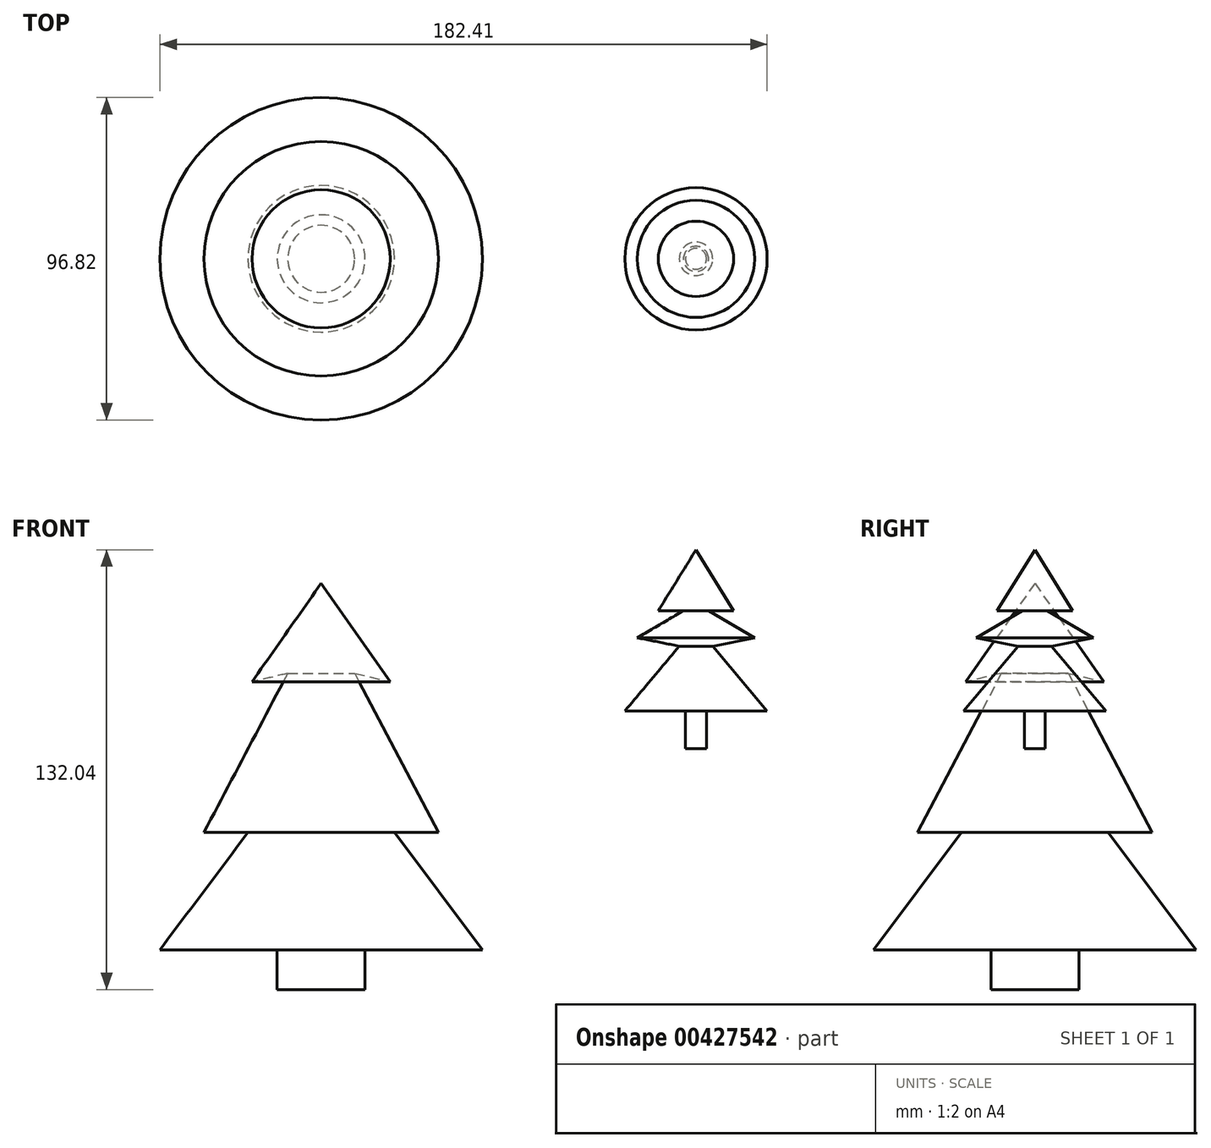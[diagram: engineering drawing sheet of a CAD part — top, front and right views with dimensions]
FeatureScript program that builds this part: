
annotation { "Feature Type Name" : "Feature", "Feature Type Description" : "" }
export const myFeature = defineFeature(function(context is Context, id is Id, definition is map)
    precondition{}
    {
        {
            var Q0;
            Q0=qCreatedBy(makeId("Front.planeOp"),FACE);
            var sketch = newSketch(context, id + "F0", { "sketchPlane" : qUnion([Q0])});
            skLineSegment(sketch, "E0", {"start": v(-35.21, 55.49) * mm, "end": v(-55.96, 25.94) * mm});
            skLineSegment(sketch, "E1", {"start": v(-55.96, 25.94) * mm, "end": v(-45.27, 28.45) * mm});
            skLineSegment(sketch, "E2", {"start": v(-45.27, 28.45) * mm, "end": v(-70.42, -19.33) * mm});
            skLineSegment(sketch, "E3", {"start": v(-70.42, -19.33) * mm, "end": v(-57.22, -19.33) * mm});
            skLineSegment(sketch, "E4", {"start": v(-57.22, -19.33) * mm, "end": v(-83.63, -54.55) * mm});
            skLineSegment(sketch, "E5", {"start": v(-83.63, -54.55) * mm, "end": v(-48.41, -54.55) * mm});
            skLineSegment(sketch, "E6", {"start": v(-35.21, -54.55) * mm, "end": v(-35.21, 55.49) * mm});
            skLineSegment(sketch, "E7", {"start": v(-48.41, -54.55) * mm, "end": v(-48.41, -66.5) * mm});
            skLineSegment(sketch, "E8", {"start": v(-48.41, -66.5) * mm, "end": v(-35.21, -66.5) * mm});
            skLineSegment(sketch, "E9", {"start": v(-35.21, -66.5) * mm, "end": v(-35.21, -54.55) * mm});
            skLineSegment(sketch, "E10", {"start": v(77.4, 65.55) * mm, "end": v(66.08, 47.31) * mm});
            skLineSegment(sketch, "E11", {"start": v(66.08, 47.31) * mm, "end": v(73.63, 47.31) * mm});
            skLineSegment(sketch, "E12", {"start": v(73.63, 47.31) * mm, "end": v(59.8, 39.14) * mm});
            skLineSegment(sketch, "E13", {"start": v(59.8, 39.14) * mm, "end": v(72.37, 36.63) * mm});
            skLineSegment(sketch, "E14", {"start": v(72.37, 36.63) * mm, "end": v(56.02, 17.13) * mm});
            skLineSegment(sketch, "E15", {"start": v(56.02, 17.13) * mm, "end": v(74.25, 17.13) * mm});
            skLineSegment(sketch, "E16", {"start": v(74.25, 17.13) * mm, "end": v(74.25, 5.82) * mm});
            skLineSegment(sketch, "E17", {"start": v(74.25, 5.82) * mm, "end": v(77.4, 5.82) * mm});
            skLineSegment(sketch, "E18", {"start": v(77.4, 5.82) * mm, "end": v(77.4, 65.55) * mm});
            skSolve(sketch);
        }
        {
            var Q0;
            Q0=makeQuery(id+"F0.imprint","IMPRINT",FACE,{"disambiguationData":[TD([[makeQuery(id+"F0.imprint","IMPRINT",EDGE,{"derivedFrom":sQuery(id+"F0.wireOp",EDGE,"E0")}),1.0]])]});
            var Q1;
            Q1=sQuery(id+"F0.wireOp",EDGE,"E6");
            revolve(context, id + "F1", {"entities" : qUnion([Q0]), "axis" : qUnion([Q1]), "revolveType" : RevolveType.FULL});
        }
        {
            var Q0;
            Q0=makeQuery(id+"F0.imprint","IMPRINT",FACE,{"disambiguationData":[TD([[makeQuery(id+"F0.imprint","IMPRINT",EDGE,{"derivedFrom":sQuery(id+"F0.wireOp",EDGE,"E10")}),1.0]])]});
            var Q1;
            Q1=sQuery(id+"F0.wireOp",EDGE,"E18");
            revolve(context, id + "F2", {"entities" : qUnion([Q0]), "axis" : qUnion([Q1]), "revolveType" : RevolveType.FULL});
        }
    });
